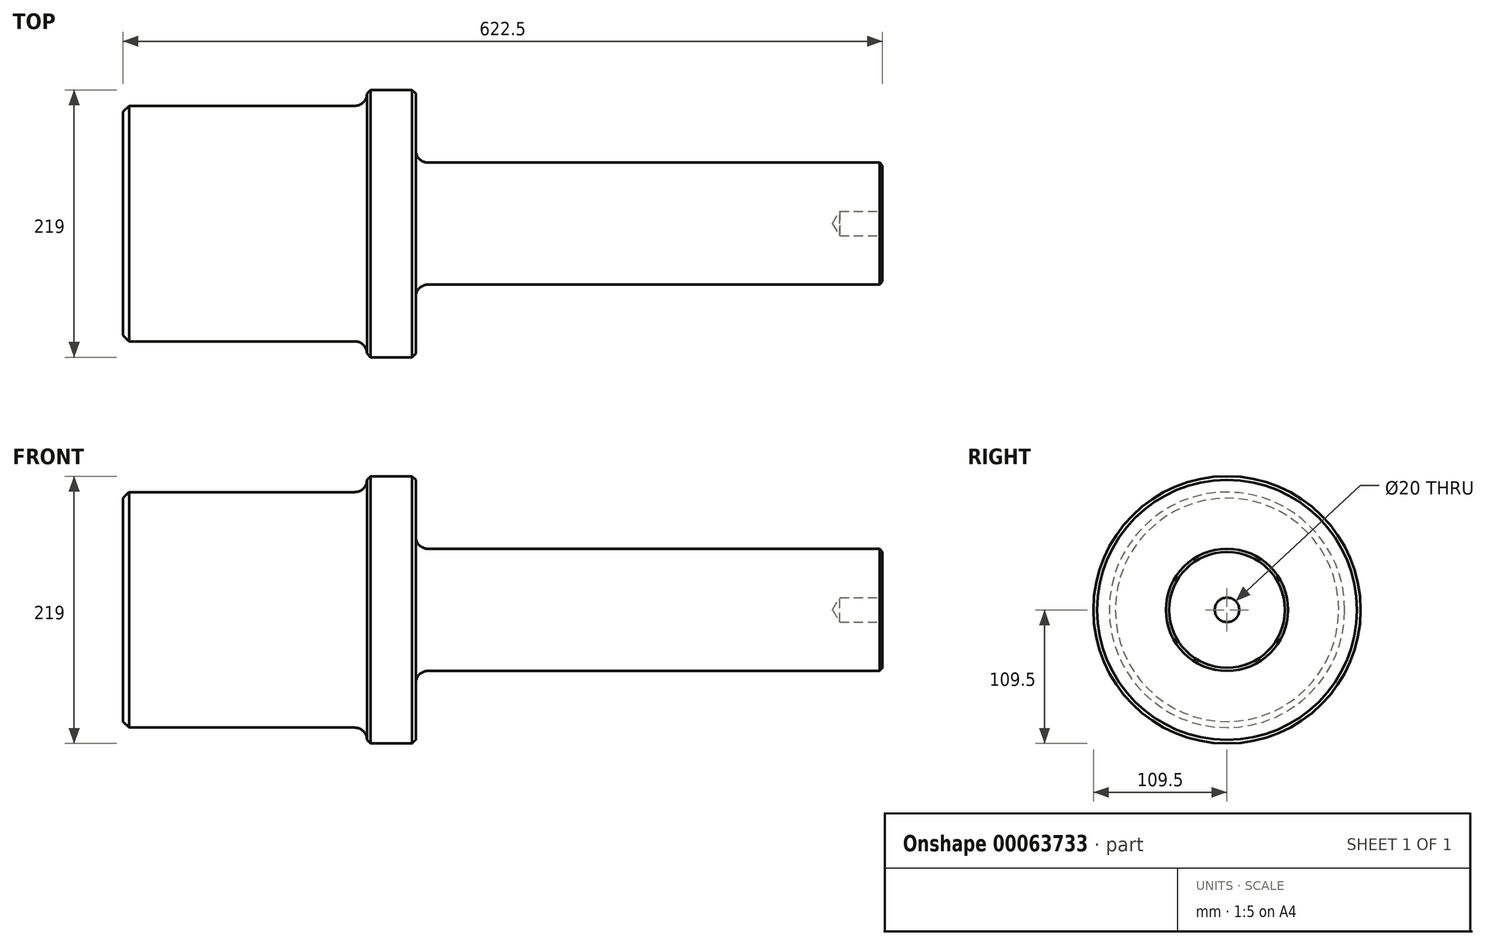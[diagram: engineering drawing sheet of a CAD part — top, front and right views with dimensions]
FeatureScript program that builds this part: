
annotation { "Feature Type Name" : "Feature", "Feature Type Description" : "" }
export const myFeature = defineFeature(function(context is Context, id is Id, definition is map)
    precondition{}
    {
        {
            var Q0;
            Q0=qCreatedBy(makeId("Front.planeOp"),FACE);
            var sketch = newSketch(context, id + "F0", { "sketchPlane" : qUnion([Q0])});
            skLineSegment(sketch, "E0", {"start": v(0, 0) * mm, "end": v(0, 96.5) * mm});
            skLineSegment(sketch, "E1", {"start": v(0, 96.5) * mm, "end": v(200, 96.5) * mm});
            skLineSegment(sketch, "E2", {"start": v(200, 96.5) * mm, "end": v(200, 109.5) * mm});
            skLineSegment(sketch, "E3", {"start": v(200, 109.5) * mm, "end": v(240, 109.5) * mm});
            skLineSegment(sketch, "E4", {"start": v(240, 109.5) * mm, "end": v(240, 50) * mm});
            skLineSegment(sketch, "E5", {"start": v(240, 50) * mm, "end": v(622.5, 50) * mm});
            skLineSegment(sketch, "E6", {"start": v(622.5, 50) * mm, "end": v(622.5, 0) * mm});
            skLineSegment(sketch, "E7", {"start": v(0, 0) * mm, "end": v(622.5, 0) * mm});
            skSolve(sketch);
        }
        {
            var Q0;
            Q0=makeQuery(id+"F0.imprint","IMPRINT",FACE,{"disambiguationData":[TD([[makeQuery(id+"F0.imprint","IMPRINT",EDGE,{"derivedFrom":sQuery(id+"F0.wireOp",EDGE,"E0")}),-1.0]])]});
            var Q1;
            Q1=sQuery(id+"F0.wireOp",EDGE,"E7");
            revolve(context, id + "F1", {"entities" : qUnion([Q0]), "axis" : qUnion([Q1]), "revolveType" : RevolveType.FULL});
        }
        {
            var Q0;
            Q0=makeQuery(id+"F1.opRevolve","SWEPT_EDGE",EDGE,{"disambiguationData":[OSD([sQuery(id+"F0.wireOp",EDGE,"E4"),sQuery(id+"F0.wireOp",EDGE,"E5")])]});
            var Q1;
            Q1=makeQuery(id+"F1.opRevolve","SWEPT_EDGE",EDGE,{"disambiguationData":[OSD([sQuery(id+"F0.wireOp",EDGE,"E1"),sQuery(id+"F0.wireOp",EDGE,"E2")])]});
            fillet(context, id + "F2", {"entities" : qUnion([Q0, Q1]), "radius" : 10 * mm, "tangentPropagation" : true, "allowEdgeOverflow" : false});
        }
        {
            var Q0;
            Q0=makeQuery(id+"F1.opRevolve","SWEPT_EDGE",EDGE,{"disambiguationData":[OSD([sQuery(id+"F0.wireOp",EDGE,"E0"),sQuery(id+"F0.wireOp",EDGE,"E1")])]});
            chamfer(context, id + "F3", {"entities" : qUnion([Q0]), "width" : 5 * mm, "tangentPropagation" : true});
        }
        {
            var Q0;
            Q0=makeQuery(id+"F1.opRevolve","SWEPT_EDGE",EDGE,{"disambiguationData":[OSD([sQuery(id+"F0.wireOp",EDGE,"E2"),sQuery(id+"F0.wireOp",EDGE,"E3")])]});
            var Q1;
            Q1=makeQuery(id+"F1.opRevolve","SWEPT_EDGE",EDGE,{"disambiguationData":[OSD([sQuery(id+"F0.wireOp",EDGE,"E3"),sQuery(id+"F0.wireOp",EDGE,"E4")])]});
            chamfer(context, id + "F4", {"entities" : qUnion([Q0, Q1]), "width" : 3 * mm, "tangentPropagation" : true});
        }
        {
            var Q0;
            Q0=makeQuery(id+"F1.opRevolve","SWEPT_EDGE",EDGE,{"disambiguationData":[OSD([sQuery(id+"F0.wireOp",EDGE,"E5"),sQuery(id+"F0.wireOp",EDGE,"E6")])]});
            chamfer(context, id + "F5", {"entities" : qUnion([Q0]), "width" : 2.5 * mm, "tangentPropagation" : true});
        }
        {
            var Q0;
            Q0=makeQuery(id+"F1.opRevolve","SWEPT_FACE",FACE,{"disambiguationData":[OSD([sQuery(id+"F0.wireOp",EDGE,"E6")])]});
            var sketch = newSketch(context, id + "F6", { "sketchPlane" : qUnion([Q0])});
            skPoint(sketch, "E8", {"position": v(0, 0) * mm});
            skSolve(sketch);
        }
        {
            var Q0;
            Q0=sQuery(id+"F6.wireOp",VERTEX,"E8");
            var Q1;
            Q1=makeQuery(id+"F1.opRevolve","SWEPT_BODY",BODY,{"disambiguationData":[OSD([sQuery(id+"F0.wireOp",EDGE,"E0"),sQuery(id+"F0.wireOp",EDGE,"E1"),sQuery(id+"F0.wireOp",EDGE,"E2"),sQuery(id+"F0.wireOp",EDGE,"E3"),sQuery(id+"F0.wireOp",EDGE,"E4"),sQuery(id+"F0.wireOp",EDGE,"E5"),sQuery(id+"F0.wireOp",EDGE,"E6"),sQuery(id+"F0.wireOp",EDGE,"E7")])]});
            hole(context, id + "F7", {"style" : HoleStyle.SIMPLE, "holeDiameter" : 20 * mm, "endStyle" : HoleEndStyle.BLIND, "holeDepth" : 35 * mm, "locations" : qUnion([Q0]), "scope" : qUnion([Q1])});
        }
        {
            var Q0;
            Q0=makeQuery(id+"F1.opRevolve","SWEPT_BODY",BODY,{"disambiguationData":[OSD([sQuery(id+"F0.wireOp",EDGE,"E0"),sQuery(id+"F0.wireOp",EDGE,"E1"),sQuery(id+"F0.wireOp",EDGE,"E2"),sQuery(id+"F0.wireOp",EDGE,"E3"),sQuery(id+"F0.wireOp",EDGE,"E4"),sQuery(id+"F0.wireOp",EDGE,"E5"),sQuery(id+"F0.wireOp",EDGE,"E6"),sQuery(id+"F0.wireOp",EDGE,"E7")])]});
            transform(context, id + "F8", {"entities" : qUnion([Q0]), "transformType" : TransformType.TRANSLATION_3D, "dx" : 0 * mm, "dy" : 0 * mm, "dz" : 0 * mm, "makeCopy" : true});
        }
        {
            var Q0;
            Q0=makeQuery(id+"F8.opPattern","COPY",BODY,{"derivedFrom":makeQuery(id+"F1.opRevolve","SWEPT_BODY",BODY,{"disambiguationData":[OSD([sQuery(id+"F0.wireOp",EDGE,"E0"),sQuery(id+"F0.wireOp",EDGE,"E1"),sQuery(id+"F0.wireOp",EDGE,"E2"),sQuery(id+"F0.wireOp",EDGE,"E3"),sQuery(id+"F0.wireOp",EDGE,"E4"),sQuery(id+"F0.wireOp",EDGE,"E5"),sQuery(id+"F0.wireOp",EDGE,"E6"),sQuery(id+"F0.wireOp",EDGE,"E7")])]}),"instanceName":"1"});
            deleteBodies(context, id + "F9", {"entities" : qUnion([Q0])});
        }
        {
            var Q0;
            Q0=makeQuery(id+"F1.opRevolve","SWEPT_BODY",BODY,{"disambiguationData":[OSD([sQuery(id+"F0.wireOp",EDGE,"E0"),sQuery(id+"F0.wireOp",EDGE,"E1"),sQuery(id+"F0.wireOp",EDGE,"E2"),sQuery(id+"F0.wireOp",EDGE,"E3"),sQuery(id+"F0.wireOp",EDGE,"E4"),sQuery(id+"F0.wireOp",EDGE,"E5"),sQuery(id+"F0.wireOp",EDGE,"E6"),sQuery(id+"F0.wireOp",EDGE,"E7")])]});
            transform(context, id + "F10", {"entities" : qUnion([Q0]), "transformType" : TransformType.TRANSLATION_3D, "dx" : 0 * mm, "dy" : 0 * mm, "dz" : 0 * mm, "makeCopy" : true});
        }
        {
            var Q0;
            Q0=makeQuery(id+"F1.opRevolve","SWEPT_BODY",BODY,{"disambiguationData":[OSD([sQuery(id+"F0.wireOp",EDGE,"E0"),sQuery(id+"F0.wireOp",EDGE,"E1"),sQuery(id+"F0.wireOp",EDGE,"E2"),sQuery(id+"F0.wireOp",EDGE,"E3"),sQuery(id+"F0.wireOp",EDGE,"E4"),sQuery(id+"F0.wireOp",EDGE,"E5"),sQuery(id+"F0.wireOp",EDGE,"E6"),sQuery(id+"F0.wireOp",EDGE,"E7")])]});
            deleteBodies(context, id + "F11", {"entities" : qUnion([Q0])});
        }
        {
            var Q0;
            Q0=makeQuery(id+"F10.opPattern","COPY",BODY,{"derivedFrom":makeQuery(id+"F1.opRevolve","SWEPT_BODY",BODY,{"disambiguationData":[OSD([sQuery(id+"F0.wireOp",EDGE,"E0"),sQuery(id+"F0.wireOp",EDGE,"E1"),sQuery(id+"F0.wireOp",EDGE,"E2"),sQuery(id+"F0.wireOp",EDGE,"E3"),sQuery(id+"F0.wireOp",EDGE,"E4"),sQuery(id+"F0.wireOp",EDGE,"E5"),sQuery(id+"F0.wireOp",EDGE,"E6"),sQuery(id+"F0.wireOp",EDGE,"E7")])]}),"instanceName":"1"});
            transform(context, id + "F12", {"entities" : qUnion([Q0]), "transformType" : TransformType.TRANSLATION_3D, "dx" : 0 * mm, "dy" : 0 * mm, "dz" : 0 * mm, "makeCopy" : true});
        }
        {
            var Q0;
            Q0=makeQuery(id+"F12.opPattern","COPY",BODY,{"derivedFrom":makeQuery(id+"F10.opPattern","COPY",BODY,{"derivedFrom":makeQuery(id+"F1.opRevolve","SWEPT_BODY",BODY,{"disambiguationData":[OSD([sQuery(id+"F0.wireOp",EDGE,"E0"),sQuery(id+"F0.wireOp",EDGE,"E1"),sQuery(id+"F0.wireOp",EDGE,"E2"),sQuery(id+"F0.wireOp",EDGE,"E3"),sQuery(id+"F0.wireOp",EDGE,"E4"),sQuery(id+"F0.wireOp",EDGE,"E5"),sQuery(id+"F0.wireOp",EDGE,"E6"),sQuery(id+"F0.wireOp",EDGE,"E7")])]}),"instanceName":"1"}),"instanceName":"1"});
            deleteBodies(context, id + "F13", {"entities" : qUnion([Q0])});
        }
    });
